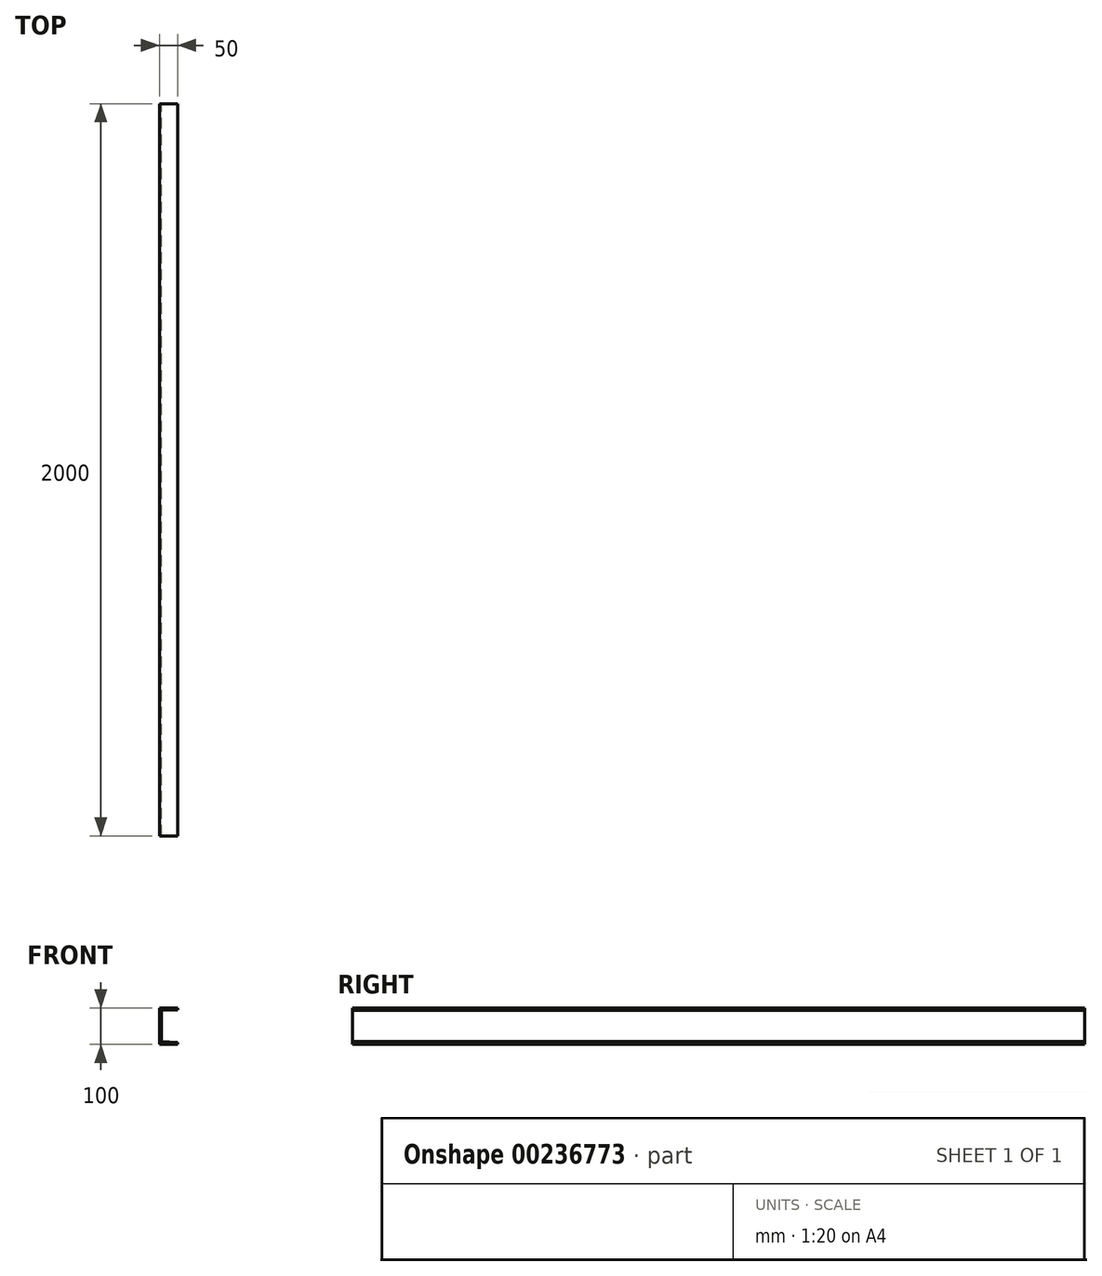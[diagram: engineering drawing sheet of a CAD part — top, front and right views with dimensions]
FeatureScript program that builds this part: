
annotation { "Feature Type Name" : "Feature", "Feature Type Description" : "" }
export const myFeature = defineFeature(function(context is Context, id is Id, definition is map)
    precondition{}
    {
        {
            var Q0;
            Q0=qCreatedBy(makeId("Front.planeOp"),FACE);
            var sketch = newSketch(context, id + "F0", { "sketchPlane" : qUnion([Q0])});
            skLineSegment(sketch, "E0.bottom", {"start": v(0, 0) * mm, "end": v(50, 0) * mm});
            skLineSegment(sketch, "E0.top", {"start": v(0, 100) * mm, "end": v(50, 100) * mm});
            skLineSegment(sketch, "E0.left", {"start": v(0, 0) * mm, "end": v(0, 100) * mm});
            skLineSegment(sketch, "E0.right", {"start": v(50, 0) * mm, "end": v(50, 5) * mm});
            skLineSegment(sketch, "E1.left", {"start": v(4.68, 71.03) * mm, "end": v(4.68, 71.03) * mm});
            skLineSegment(sketch, "E1.right", {"start": v(12.2, 71.03) * mm, "end": v(12.2, 71.03) * mm});
            skLineSegment(sketch, "E2", {"start": v(6, 8.46) * mm, "end": v(50, 5) * mm});
            skLineSegment(sketch, "E3", {"start": v(6, 8.46) * mm, "end": v(6, 93.46) * mm});
            skLineSegment(sketch, "E4", {"start": v(6, 93.46) * mm, "end": v(50, 95) * mm});
            skLineSegment(sketch, "E5.trimOffspring", {"start": v(50, 95) * mm, "end": v(50, 100) * mm});
            skSolve(sketch);
        }
        {
            var Q0;
            Q0=makeQuery(id+"F0.imprint","IMPRINT",FACE,{"disambiguationData":[TD([[makeQuery(id+"F0.imprint","IMPRINT",EDGE,{"derivedFrom":sQuery(id+"F0.wireOp",EDGE,"E0.bottom")}),1.0]])]});
            extrude(context, id + "F1", {"entities" : qUnion([Q0]), "depth" : 2000 * mm, "offsetDistance" : 25 * mm});
        }
    });
